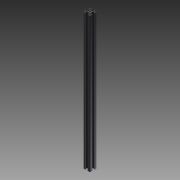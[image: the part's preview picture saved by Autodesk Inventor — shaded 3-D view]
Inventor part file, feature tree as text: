
AUTODESK INVENTOR PART (.ipt)
format: ipt  version: 2011 SP1 (Build 150282100, 282)  size: 186,368 bytes
history: native  units: mm
features: other x21, sketch x3, hole x2, extrude x1, pattern_linear x1
ambient origin geometry x8: Origin, YZ Plane, XZ Plane, XY Plane, X Axis, Y Axis, Z Axis, Center Point
bodies: Solid1 (feature_tree)
feature tree (28):
  extrude  "Extrusion1"  Depth=20.0mm
  hole  "Hole1"  [1 undecoded]
  hole  "Hole2"  [1 undecoded]
  pattern_linear  "Rectangular Pattern1"  [2 undecoded]
  other  "C1_XY"
  other  "C1_YZ"
  other  "C1_ZX"
  other  "C1_X"
  other  "C1_Y"
  other  "C1_Z"
  other  "C1_Center"
  other  "to_frame_cap1_XY"
  other  "to_frame_cap1_YZ"
  other  "to_frame_cap1_ZX"
  other  "to_frame_cap1_X"
  other  "to_frame_cap1_Y"
  other  "to_frame_cap1_Z"
  other  "to_frame_cap1_Center"
  other  "to_frame_cap2_XY"
  other  "to_frame_cap2_YZ"
  other  "to_frame_cap2_ZX"
  other  "to_frame_cap2_X"
  other  "to_frame_cap2_Y"
  other  "to_frame_cap2_Z"
  other  "to_frame_cap2_Center"
  sketch  "Sketch_1"  dims[d0=600.0mm d1=0.0mm]
  sketch  "Sketch2"  dims[d2=6.8mm d3=6.0mm d4=4.0mm d5=2.0mm d6=90.0deg d7=600.0mm d8=0.0mm]
  sketch  "Sketch3"  dims[d9=4.2mm d10=6.0mm d11=4.0mm d12=2.0mm d13=90.0deg d14=600.0mm d15=0.0mm d16=20.0mm d18=23.2mm d19=20.0mm d21=23.2mm d22=0.0mm d23=0.0mm d24=0.0mm]
note: 4 required parameter values undecoded (feature->parameter linkage not recoverable at this tier; creation-order binding heuristic only, values carry confidence <= 0.55)
